# Revit family: Window_Curtain_Wall-Single_Hung-Traco-TR_9103-Heavy_Commercial
name_source: partatom
category: Windows
revit_build: Autodesk Revit 2015 (Build: 20140905_0730(x64)
units: mm (PartAtom-declared; Revit-internal decimal feet)

## types (3) — shared parameters
Allowable Air Infiltration Maximum = 0.3 @ 6.2 PSF
Assembly Code = B2020110
Condensation Resistance = 0.0000 psf
Depth = 0' - 3 1/4"
Description = Heavy Commercial, Single Hung, Side Load
Designation = AAMA/WDMA/CSA 101/I.S.2/A-440-05: H-AW50 And AAMA/WDMA/CSA 101/I.S.2/A-440-08: AW-PG50-H
Forced Entry Resistance = TYPE A: GRADE 10
Frame Material = Aluminum - Traco - Anodized - Gray
Glazing Material = Glass - Traco - Clear
Has Muntins = No
Head Width = 0' - 1"
Height Maximum = 10' - 0"
Height Minimum = 2' - 0"
Keynote = 08500
Manufacturer = Traco
Product Documentation Link = http://www.alcoa.com
Product Page URL = http://www.alcoa.com
Product data url = https://bimobject.com
Rail Width = 0' - 2"
Screen Material = Aluminum - Traco - Screen
Sill Width = 0' - 3 1/2"
Test Size = 60" X 99"
U Factor = .45 Per NFRC 100
URL = http://www.alcoa.com
Uniform Load Deflection = 50.0000 psf
Uniform Load Structural = 75.0000 psf
Water Resistance = 15.0000 psf
Width Maximum = 10' - 0"
Width Minimum = 2' - 0"

## per-type parameters (varying)
| type | Glazing Thickness | Model | Type Comments |
| TR-9103 - SH/Fixed Top | 0' - 1" | TR-9103 | Single Hung 3-Lite Standard |
| TR-9103 - SH/Fixed-Top - w/Class 5 Balances | 0' - 1" | TR-9103U | Single Hung 3-Lite Class 5 Balances |
| TR-9103 - SH/Fixed-Top - Single Glazed | 0' - 0 1/4" | TR-9103 | Single Hung 3-Lite Single Glazed |

## geometry (parser evidence)
native form markers: Blend x4, Sweep x10
no freeform markers — native parametric forms only
